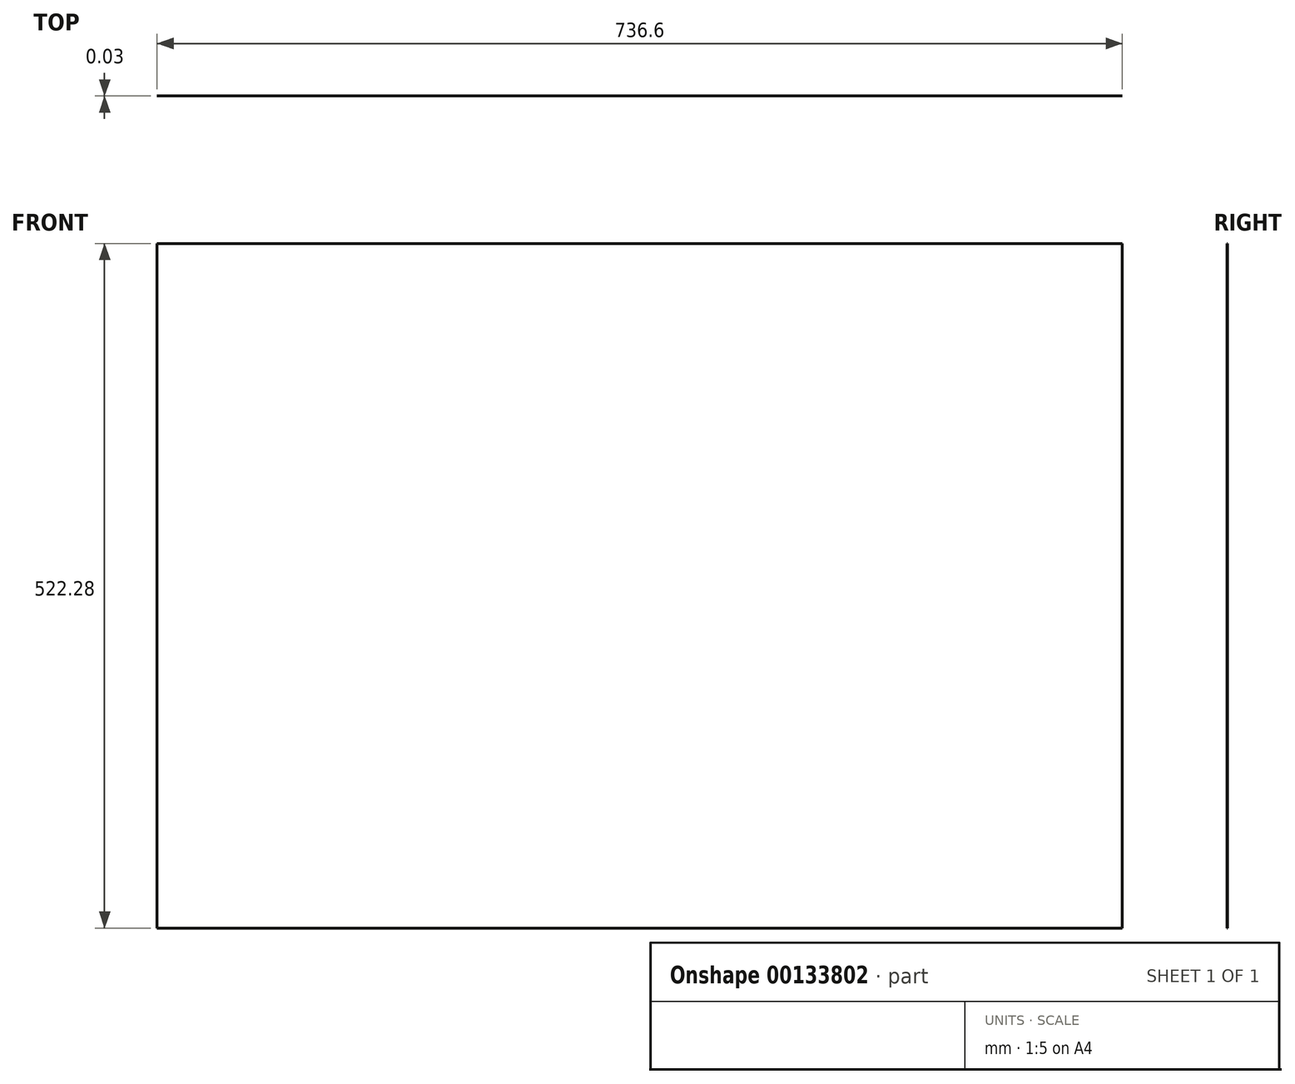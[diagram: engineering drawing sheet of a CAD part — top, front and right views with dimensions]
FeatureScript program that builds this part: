
annotation { "Feature Type Name" : "Feature", "Feature Type Description" : "" }
export const myFeature = defineFeature(function(context is Context, id is Id, definition is map)
    precondition{}
    {
        {
            var Q0;
            Q0=qCreatedBy(makeId("Front.planeOp"),FACE);
            var sketch = newSketch(context, id + "F0", { "sketchPlane" : qUnion([Q0])});
            skLineSegment(sketch, "E0.bottom", {"start": v(368.3, -261.14) * mm, "end": v(-368.3, -261.14) * mm});
            skLineSegment(sketch, "E0.top", {"start": v(368.3, 261.14) * mm, "end": v(-368.3, 261.14) * mm});
            skLineSegment(sketch, "E0.left", {"start": v(368.3, -261.14) * mm, "end": v(368.3, 261.14) * mm});
            skLineSegment(sketch, "E0.right", {"start": v(-368.3, -261.14) * mm, "end": v(-368.3, 261.14) * mm});
            skPoint(sketch, "E0.middle", {"position": v(0, 0) * mm});
            skSolve(sketch);
        }
        {
            var Q0;
            Q0 = qSketchRegion(id + "F0", true);
            extrude(context, id + "F1", {"entities" : qUnion([Q0]), "depth" : 0.03 * mm});
        }
    });
